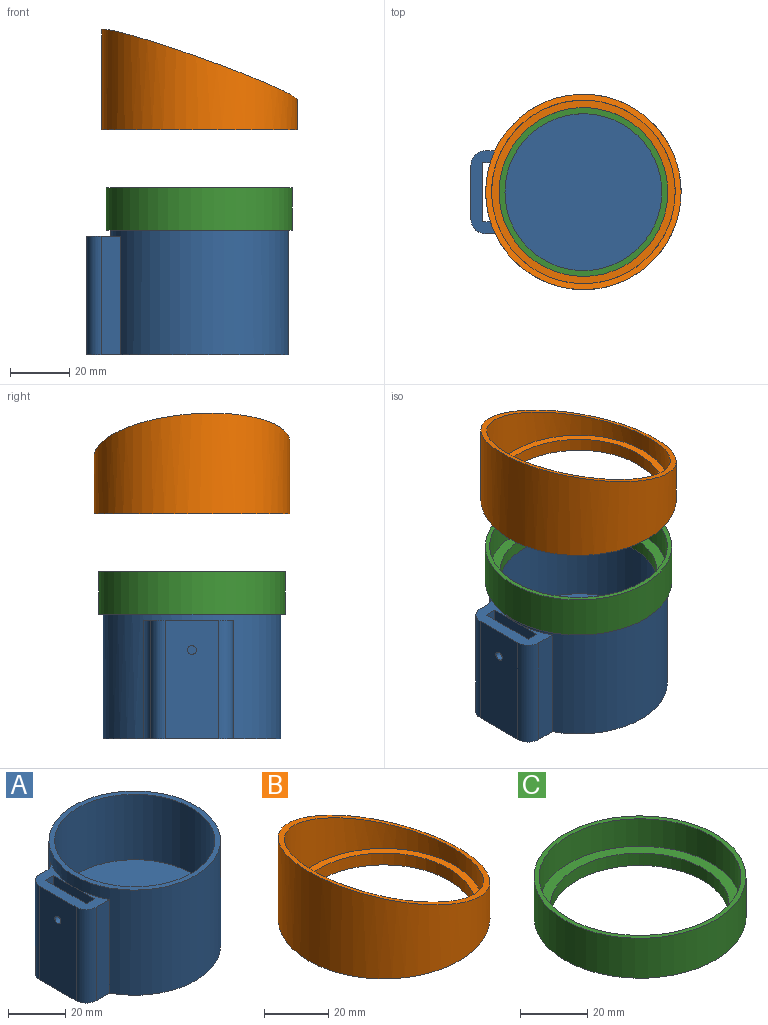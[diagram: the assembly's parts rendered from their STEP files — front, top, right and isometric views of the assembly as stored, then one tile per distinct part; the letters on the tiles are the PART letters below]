
ASSEMBLY  parts=3 mates=2
PART A: 19 faces, bbox 68x60x45 mm
  f0: cylinder r=30mm len=60mm, axis (0,0,-1), area 7211.1mm2, adj f1,f2,f11,f14,f17
  f1: plane 68x60mm, normal (0,0,-1), area 530.5mm2, adj f0,f6,f7,f8,f9,f10,f11,f12
  f2: plane 60x60mm, normal (0,0,1), area 364.4mm2, adj f0,f3
  f3: cylinder r=28mm len=56mm, axis (0,0,-1), area 4926mm2, adj f2,f4
  f4: plane 56x56mm, normal (0,0,1), area 2463mm2, adj f3
  f5: plane 56x56mm, normal (0,0,-1), area 2463mm2, adj f6
  f6: cylinder r=28mm len=56mm, axis (0,0,-1), area 2638.9mm2, adj f1,f5
  f7: plane 40x20mm, normal (-1,0,0), area 800mm2, adj f1,f8,f9,f14
  f8: plane 40x4mm, normal (0,1,0), area 160mm2, adj f1,f7,f13,f14
  f9: plane 40x4mm, normal (0,-1,0), area 160mm2, adj f1,f7,f13,f14
  f10: plane 40x3.61mm, normal (0,1,0), area 144.2mm2, adj f1,f14,f16,f17
  f11: plane 40x6.47mm, normal (0,-1,0), area 258.7mm2, adj f0,f1,f14,f15
  f12: plane 40x18mm, normal (-1,0,0), area 712.9mm2, adj f1,f14,f15,f16,f18
  f13: plane 40x20mm, normal (1,0,0), area 792.9mm2, adj f1,f8,f9,f14,f18
  f14: plane 30.29x12.81mm, normal (0,0,1), area 166.1mm2, adj f0,f7,f8,f9,f10,f11,f12,f13
  f15: cylinder r=5mm len=40mm, axis (0,0,-1), area 314.2mm2, adj f1,f11,f12,f14
  f16: cylinder r=5mm len=40mm, axis (0,0,-1), area 314.2mm2, adj f1,f10,f12,f14
  f17: cylinder r=5mm len=40mm, axis (0,0,-1), area 199.4mm2, adj f0,f1,f10,f14
  f18: cylinder r=1.5mm len=4mm, axis (-1,0,0), area 37.7mm2, adj f12,f13
PART B: 10 faces, bbox 71.1x71.1x39.1 mm
  f0: cylinder r=33mm len=66mm, axis (0,0,-1), area 4563.9mm2, adj f6,f9
  f1: cylinder r=31mm len=62mm, axis (0,0,-1), area 3410.8mm2, adj f7,f9
  f2: plane 60x60mm, normal (0,0,-1), area 275.7mm2, adj f3,f8
  f3: cylinder r=30mm len=60mm, axis (0,0,-1), area 565.5mm2, adj f2,f4
  f4: plane 63x63mm, normal (0,0,-1), area 289.8mm2, adj f3,f5
  f5: cylinder r=31.5mm len=63mm, axis (0,0,-1), area 593.8mm2, adj f4,f6
  f6: plane 66x66mm, normal (0,0,-1), area 303.9mm2, adj f0,f5
  f7: plane 62x62mm, normal (0,0,1), area 467.3mm2, adj f1,f8
  f8: cylinder r=28.5mm len=57mm, axis (0,0,-1), area 805.8mm2, adj f2,f7
  f9: plane 71.05x71.05mm, normal (0.34,0,0.94), area 427.9mm2, adj f0,f1
PART C: 10 faces, bbox 63x63x14.5 mm
  f0: cylinder r=31.5mm len=63mm, axis (0,0,-1), area 2869.8mm2, adj f1,f9
  f1: plane 63x63mm, normal (0,0,1), area 289.8mm2, adj f0,f2
  f2: cylinder r=30mm len=60mm, axis (0,0,-1), area 1885mm2, adj f1,f3
  f3: plane 60x60mm, normal (0,0,1), area 621.2mm2, adj f2,f4
  f4: cylinder r=26.5mm len=53mm, axis (0,0,-1), area 749.3mm2, adj f3,f5
  f5: plane 56x56mm, normal (0,0,-1), area 256.8mm2, adj f4,f6
  f6: cylinder r=28mm len=56mm, axis (0,0,-1), area 527.8mm2, adj f5,f7
  f7: plane 60x60mm, normal (0,0,-1), area 364.4mm2, adj f6,f8
  f8: cylinder r=30mm len=60mm, axis (0,0,-1), area 565.5mm2, adj f7,f9
  f9: plane 63x63mm, normal (0,0,-1), area 289.8mm2, adj f0,f8
PLACE A at identity fixed
PLACE B rot(axis=(0,0,1),11.8deg) t=(0,0,22.48)mm
PLACE C at identity
MATE cylindrical C.f0 <-> A.f0  axis (0,0,-1) through (0,0,30)mm
MATE cylindrical C.f0 <-> B.f0  axis (0,0,1) through (0,0,41.5)mm
